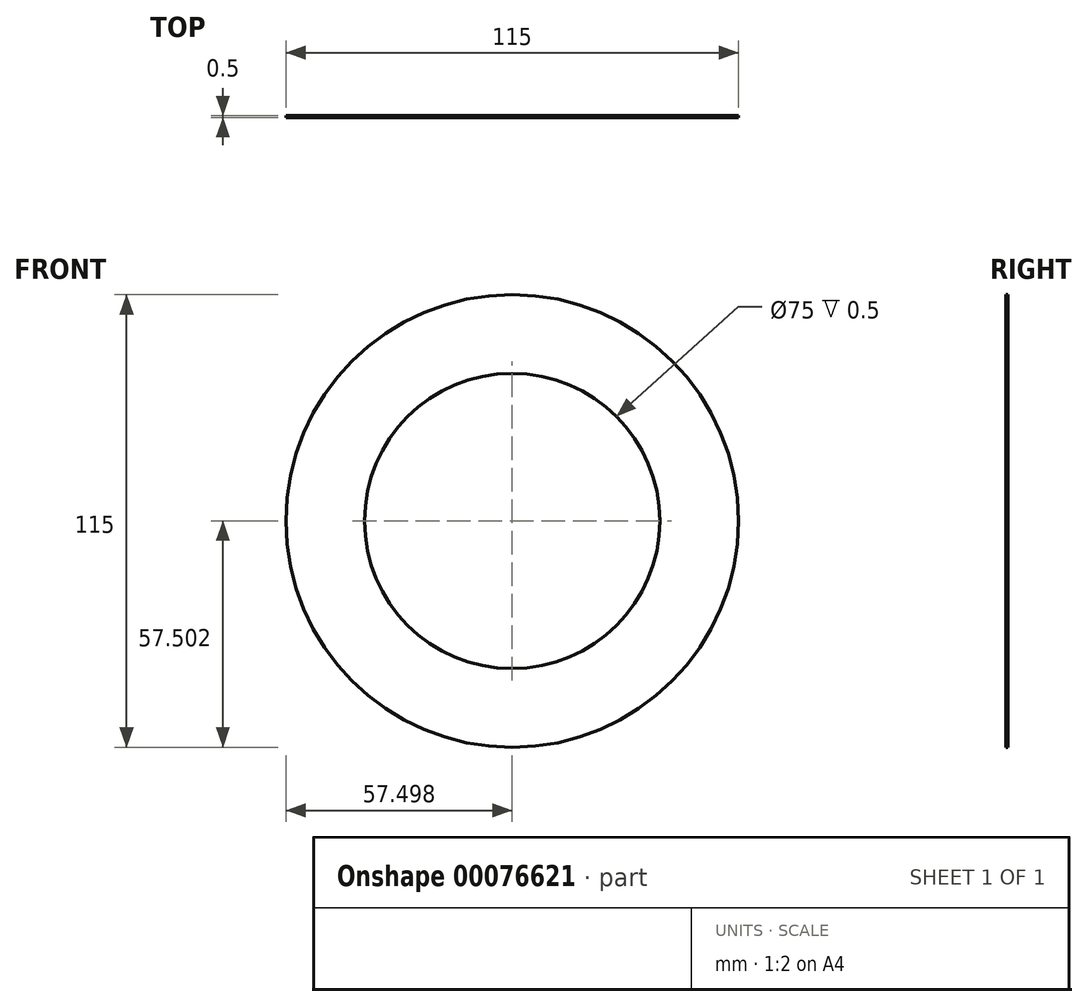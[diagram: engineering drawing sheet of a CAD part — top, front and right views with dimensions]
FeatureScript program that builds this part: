
annotation { "Feature Type Name" : "Feature", "Feature Type Description" : "" }
export const myFeature = defineFeature(function(context is Context, id is Id, definition is map)
    precondition{}
    {
        {
            var Q0;
            Q0=qCreatedBy(makeId("Front.planeOp"),FACE);
            var sketch = newSketch(context, id + "F0", { "sketchPlane" : qUnion([Q0])});
            skCircle(sketch, "E0", {"center": v(-37.38, 20.11) * mm, "radius": 37.5 * mm});
            skCircle(sketch, "E1", {"center": v(-37.38, 20.11) * mm, "radius": 57.5 * mm});
            skSolve(sketch);
        }
        {
            var Q0;
            Q0 = qSketchRegion(id + "F0", true);
            var Q1;
            Q1=makeQuery(id+"F0.imprint","IMPRINT",FACE,{"disambiguationData":[TD([[makeQuery(id+"F0.imprint","IMPRINT",EDGE,{"derivedFrom":sQuery(id+"F0.wireOp",EDGE,"E0")}),-1.0]])]});
            extrude(context, id + "F1", {"entities" : qUnion([Q0, Q1]), "depth" : .5 * mm});
        }
    });
